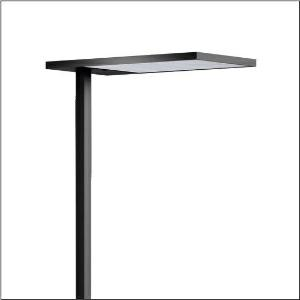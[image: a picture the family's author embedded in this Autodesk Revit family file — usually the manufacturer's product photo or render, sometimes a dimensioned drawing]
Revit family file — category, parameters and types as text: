
# Revit family: silica_r__21_floor_r_51mx53sg4db_4ec3
name_source: partatom
category: Lighting Fixtures
units: mm (PartAtom-declared; Revit-internal decimal feet)

## family parameters
Cut with Voids When Loaded = No
Host = Face
Light Source = No
Part Type = Normal
Room Calculation Point = No
Round Connector Dimension = Use Diameter
Shared = No

## types (1)
- Silica® 21 Floor R (1 x LED, 15000 lm, 106.4 W, 4000K)
    Apparent Load = 106 VA
    CIE Flux Codes = 54 86 97 13 100
    Color Rendering = 80
    Color Temperature = 4000K
    Default Elevation = 1800 mm
    Description = Silica® 21 Floor R, floorstanding luminaire, of PMMA, primary optical cover: prismatic diffuser, of PMMA, CAT 2 (L<= 3000cd/m²), light emission: indirect/direct distribution, primary light characteristic: symmetric, primary optical cover: cover panel, of PMMA, installation type: not mounted, LED, rated luminous flux: 15.000lm, luminous efficacy: 141lm/W, light colour: 840, colour temperature: 4000K, daylight-dependent control, mains connection: 230V, AC, 50/60Hz, connection cable pre-assembled, cable length: 2,5m, rated input power: 106.4W, luminaire head, of aluminium, coated, jet black (RAL 9005), length: 671mm, width: 330mm, height: 2010mm, supporting column, angular, of aluminium, coated, jet black (RAL 9005), baseplate, of steel, coated, jet black (RAL 9005), protection rating (complete): IP20, insulation class (complete): insulation class I (protective earthing), certification: CE, standard: EN 50419, packaging unit: 1 piece
    Height = 18 mm
    Lamp = 1 x LED
    Lamp Light Flux = 15000 lm
    Lamp Power = 106.4 W
    Lamp count = 1
    Length = 650 mm
    Luminous efficacy = 141 lm/W
    Manufacturer = Siteco
    ModVariant = No
    Model = 51MX53SG4DB
    Mounting Place = Floor
    Mounting Type = Freestanding
    Number of Poles = 1
    OnlyDefault = Yes
    Power Factor = 1
    Product Name = Silica® 21 Floor R
    Product group = floorstanding luminaire
    ProductGroupID = 1302
    Protection Class = Protection class I
    Protection Degree = IP 20
    RLX_Detail_Level = 1
    RLX_Emergency_Light_Flux = 0 lm
    RLX_Emergency_Type = 0
    RLX_Emergency_Type_DB = No
    RlxData = <blob elided: 22077 chars, md5=2f24e8c1>
    Socket = socket
    Standby Power = 0 W
    System Light Flux = 15000 lm
    System Power = 106 W
    Type Comments = Product without accessories
    Type Image = l_1007011.jpg
    URL = http://relux.com
    VarID = ---
    Voltage = 0 V
    Weight = 0.00 kg
    Width = 350 mm

## geometry (parser evidence)
native form markers: Blend x4, Sweep x17
no freeform markers — native parametric forms only
